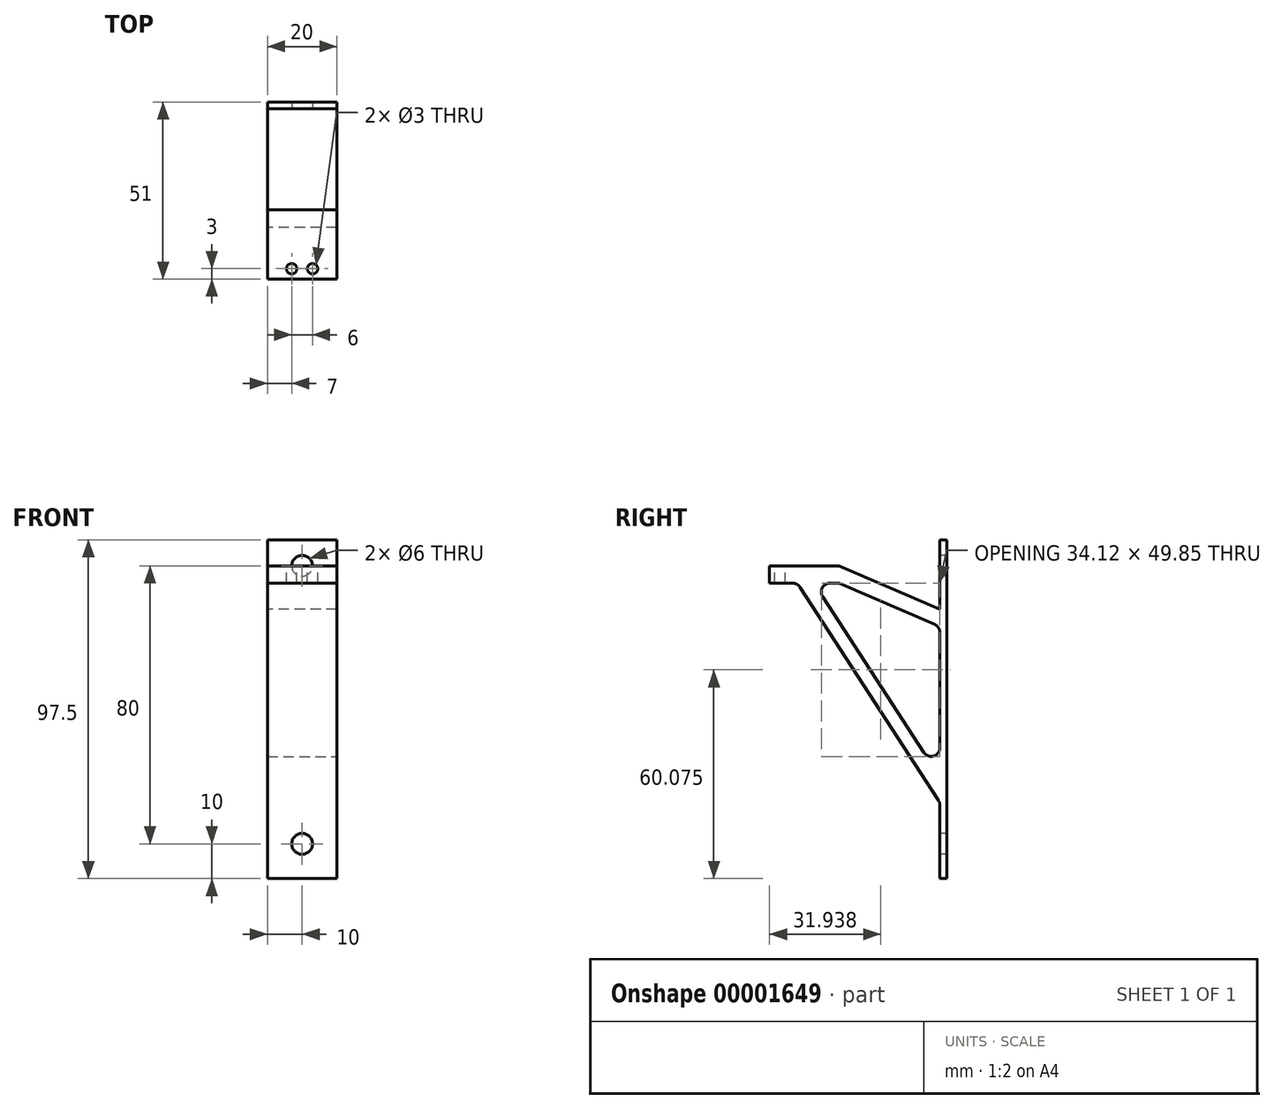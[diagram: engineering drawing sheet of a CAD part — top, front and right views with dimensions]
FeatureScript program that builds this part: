
annotation { "Feature Type Name" : "Feature", "Feature Type Description" : "" }
export const myFeature = defineFeature(function(context is Context, id is Id, definition is map)
    precondition{}
    {
        {
            var Q0;
            Q0=qCreatedBy(makeId("Right.planeOp"),FACE);
            var sketch = newSketch(context, id + "F0", { "sketchPlane" : qUnion([Q0])});
            skLineSegment(sketch, "E0", {"start": v(-51, 90) * mm, "end": v(-51, 85) * mm});
            skLineSegment(sketch, "E1", {"start": v(-51, 85) * mm, "end": v(-43, 85) * mm});
            skLineSegment(sketch, "E2", {"start": v(-43, 85) * mm, "end": v(-2, 21.87) * mm});
            skLineSegment(sketch, "E3", {"start": v(-2, 21.87) * mm, "end": v(-2, 0) * mm});
            skLineSegment(sketch, "E4", {"start": v(-2, 0) * mm, "end": v(0, 0) * mm});
            skLineSegment(sketch, "E5", {"start": v(-38.23, 85) * mm, "end": v(-2, 29.2) * mm});
            skLineSegment(sketch, "E6", {"start": v(-2, 29.2) * mm, "end": v(-2, 72.5) * mm});
            skLineSegment(sketch, "E7.top", {"start": v(0, 97.5) * mm, "end": v(-2, 97.5) * mm});
            skLineSegment(sketch, "E7.left", {"start": v(0, 0) * mm, "end": v(0, 97.5) * mm});
            skLineSegment(sketch, "E7.right", {"start": v(-2, 77.5) * mm, "end": v(-2, 97.5) * mm});
            skLineSegment(sketch, "E8", {"start": v(-2, 77.5) * mm, "end": v(-31, 90) * mm});
            skLineSegment(sketch, "E9", {"start": v(-31, 90) * mm, "end": v(-51, 90) * mm});
            skLineSegment(sketch, "E10", {"start": v(-38.23, 85) * mm, "end": v(-31, 85) * mm});
            skLineSegment(sketch, "E11", {"start": v(-31, 85) * mm, "end": v(-2, 72.5) * mm});
            skSolve(sketch);
        }
        {
            var Q0;
            Q0 = qSketchRegion(id + "F0", true);
            extrude(context, id + "F1", {"entities" : qUnion([Q0]), "depth" : 20 * mm});
        }
        {
            var Q0;
            Q0=makeQuery(id+"F1.opExtrude","SWEPT_EDGE",EDGE,{"disambiguationData":[OSD([sQuery(id+"F0.wireOp",EDGE,"E1"),sQuery(id+"F0.wireOp",EDGE,"E2")])]});
            var Q1;
            Q1=makeQuery(id+"F1.opExtrude","SWEPT_EDGE",EDGE,{"disambiguationData":[OSD([sQuery(id+"F0.wireOp",EDGE,"E2"),sQuery(id+"F0.wireOp",EDGE,"E3")])]});
            var Q2;
            Q2=makeQuery(id+"F1.opExtrude","SWEPT_EDGE",EDGE,{"disambiguationData":[OSD([sQuery(id+"F0.wireOp",EDGE,"E6"),sQuery(id+"F0.wireOp",EDGE,"773b51c7-71e7-4640-8ecd-1af9c694fd57")])]});
            var Q3;
            Q3=makeQuery(id+"F1.opExtrude","SWEPT_EDGE",EDGE,{"disambiguationData":[OSD([sQuery(id+"F0.wireOp",EDGE,"E5"),sQuery(id+"F0.wireOp",EDGE,"773b51c7-71e7-4640-8ecd-1af9c694fd57")])]});
            var Q4;
            Q4=makeQuery(id+"F1.opExtrude","SWEPT_EDGE",EDGE,{"disambiguationData":[OSD([sQuery(id+"F0.wireOp",EDGE,"E5"),sQuery(id+"F0.wireOp",EDGE,"E6")])]});
            fillet(context, id + "F2", {"entities" : qUnion([Q0, Q1, Q2, Q3, Q4]), "radius" : 2.5 * mm, "tangentPropagation" : true, "allowEdgeOverflow" : false});
        }
        {
            var Q0;
            Q0=makeQuery(id+"F1.opExtrude","SWEPT_FACE",FACE,{"disambiguationData":[OSD([sQuery(id+"F0.wireOp",EDGE,"E6")])]});
            var sketch = newSketch(context, id + "F3", { "sketchPlane" : qUnion([Q0])});
            skLineSegment(sketch, "E12", {"start": v(10, 97.5) * mm, "end": v(10, 0) * mm, "construction": true});
            skCircle(sketch, "E13", {"center": v(10, 10) * mm, "radius": 3 * mm});
            skCircle(sketch, "E14", {"center": v(10, 90) * mm, "radius": 3 * mm});
            skSolve(sketch);
        }
        {
            var Q0;
            Q0 = qSketchRegion(id + "F3", true);
            extrude(context, id + "F4", {"entities" : qUnion([Q0]), "operationType" : NewBodyOperationType.REMOVE, "oppositeDirection" : true, "depth" : 25 * mm});
        }
        {
            var Q0;
            Q0=makeQuery(id+"F1.opExtrude","SWEPT_FACE",FACE,{"disambiguationData":[OSD([sQuery(id+"F0.wireOp",EDGE,"E9")])]});
            var sketch = newSketch(context, id + "F5", { "sketchPlane" : qUnion([Q0])});
            skLineSegment(sketch, "E15", {"start": v(10, -51) * mm, "end": v(10, -31) * mm, "construction": true});
            skCircle(sketch, "E16", {"center": v(7, -48) * mm, "radius": 1.5 * mm});
            skCircle(sketch, "E17.0.MirrorC", {"center": v(13, -48) * mm, "radius": 1.5 * mm});
            skSolve(sketch);
        }
        {
            var Q0;
            Q0 = qSketchRegion(id + "F5", true);
            extrude(context, id + "F6", {"entities" : qUnion([Q0]), "operationType" : NewBodyOperationType.REMOVE, "endBound" : BoundingType.UP_TO_NEXT, "oppositeDirection" : true, "depth" : 25 * mm});
        }
    });
